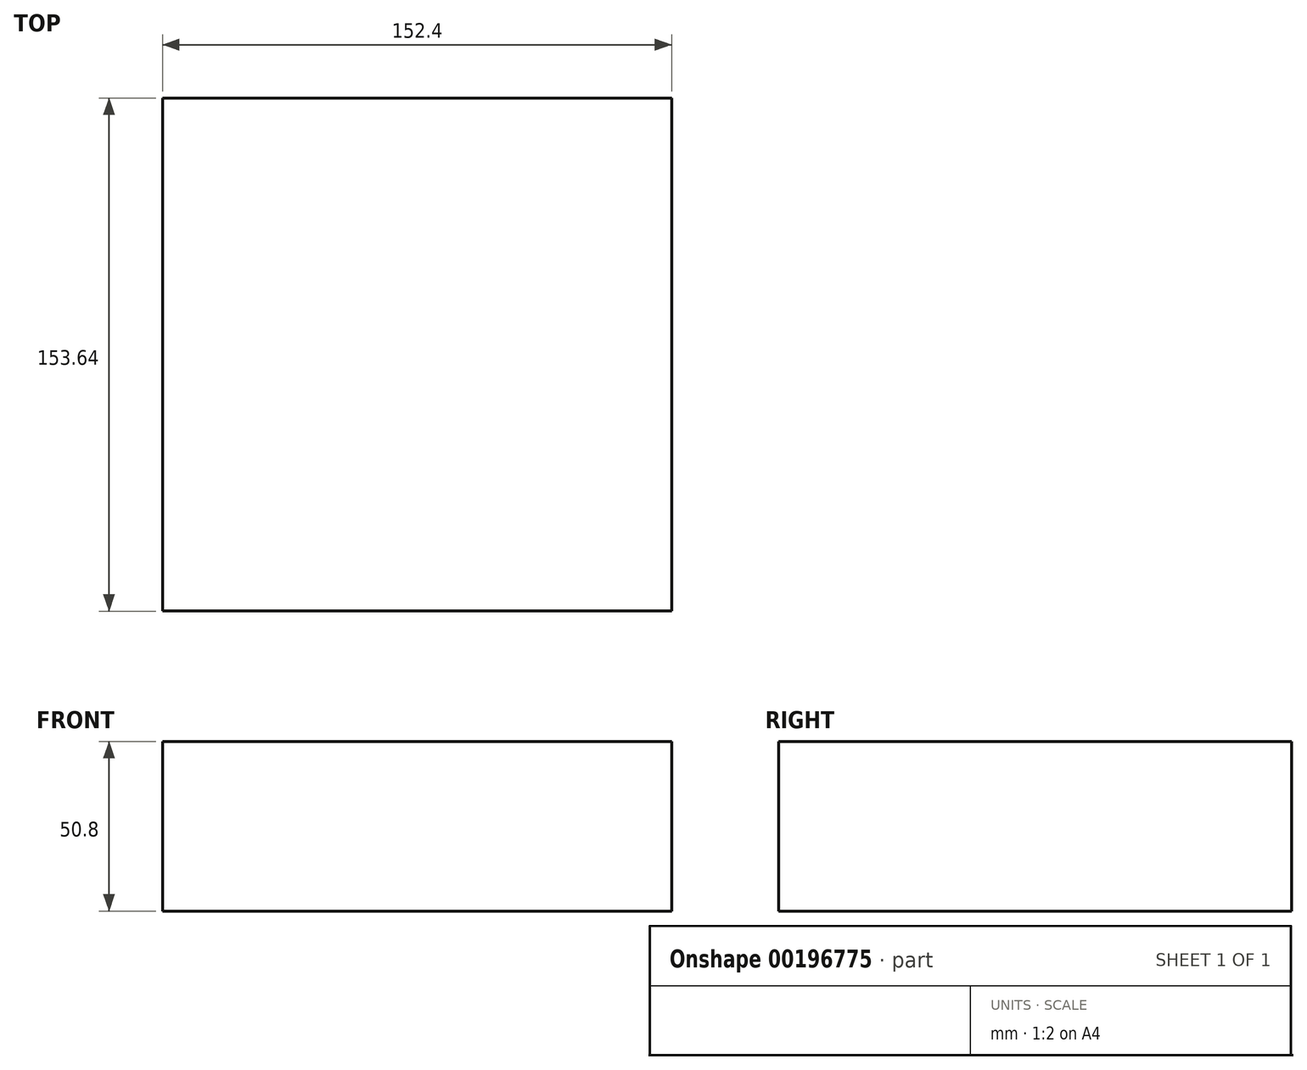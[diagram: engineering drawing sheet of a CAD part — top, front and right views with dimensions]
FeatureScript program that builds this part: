
annotation { "Feature Type Name" : "Feature", "Feature Type Description" : "" }
export const myFeature = defineFeature(function(context is Context, id is Id, definition is map)
    precondition{}
    {
        {
            var Q0;
            Q0=qCreatedBy(makeId("Top.planeOp"),FACE);
            var sketch = newSketch(context, id + "F0", { "sketchPlane" : qUnion([Q0])});
            skLineSegment(sketch, "E0.bottom", {"start": v(-76.2, 76.82) * mm, "end": v(76.2, 76.82) * mm});
            skLineSegment(sketch, "E0.top", {"start": v(-76.2, -76.82) * mm, "end": v(76.2, -76.82) * mm});
            skLineSegment(sketch, "E0.left", {"start": v(-76.2, 76.82) * mm, "end": v(-76.2, -76.82) * mm});
            skLineSegment(sketch, "E0.right", {"start": v(76.2, 76.82) * mm, "end": v(76.2, -76.82) * mm});
            skPoint(sketch, "E0.middle", {"position": v(0, 0) * mm});
            skSolve(sketch);
        }
        {
            var Q0;
            Q0 = qSketchRegion(id + "F0", true);
            extrude(context, id + "F1", {"entities" : qUnion([Q0]), "depth" : 50.8 * mm});
        }
        {
            var Q0;
            Q0 = qSketchRegion(id + "F0", true);
            extrude(context, id + "F2", {"entities" : qUnion([Q0]), "operationType" : NewBodyOperationType.ADD, "depth" : 25.4 * mm});
        }
    });
